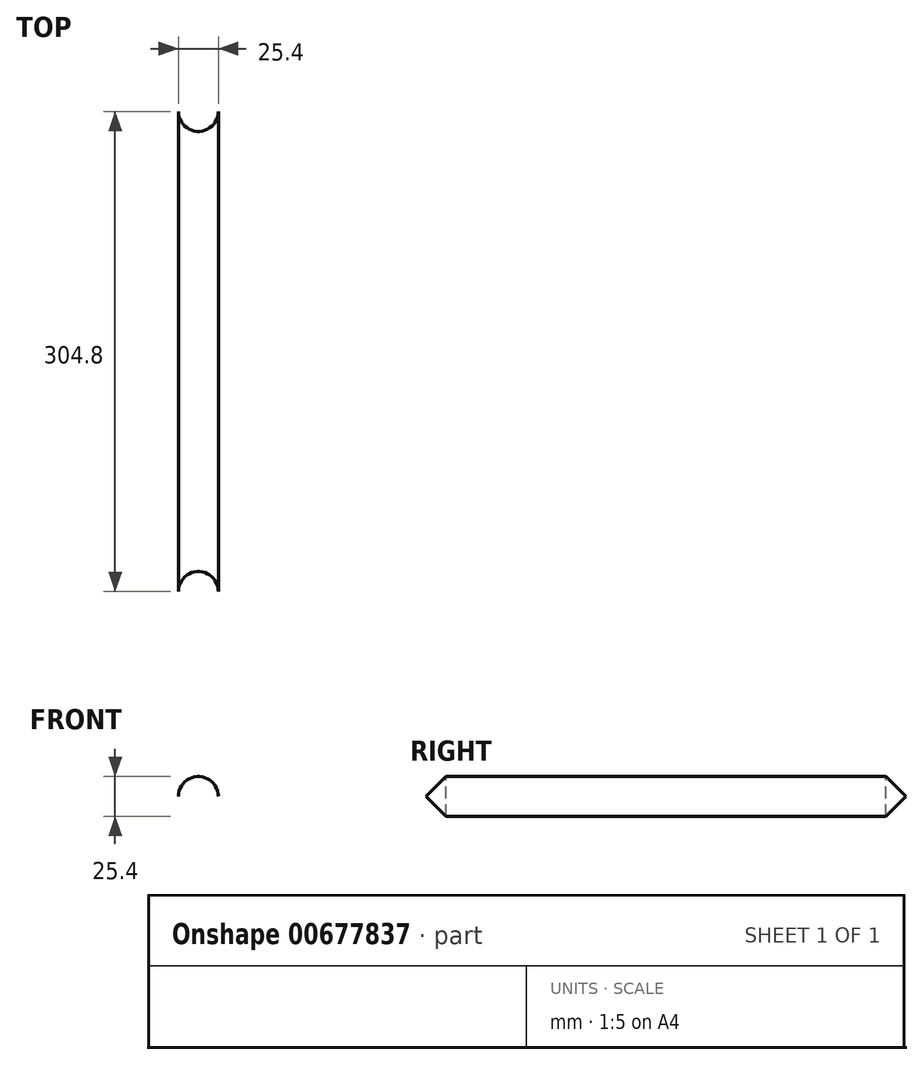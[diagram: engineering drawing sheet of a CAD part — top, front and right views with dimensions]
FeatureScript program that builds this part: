
annotation { "Feature Type Name" : "Feature", "Feature Type Description" : "" }
export const myFeature = defineFeature(function(context is Context, id is Id, definition is map)
    precondition{}
    {
        {
            var Q0;
            Q0=qCreatedBy(makeId("Front.planeOp"),FACE);
            var sketch = newSketch(context, id + "F0", { "sketchPlane" : qUnion([Q0])});
            skCircle(sketch, "E0", {"center": v(0, 0) * mm, "radius": 12.7 * mm});
            skSolve(sketch);
        }
        {
            var Q0;
            Q0=makeQuery(id+"F0.imprint","IMPRINT",FACE,{"disambiguationData":[TD([[makeQuery(id+"F0.imprint","IMPRINT",EDGE,{"derivedFrom":sQuery(id+"F0.wireOp",EDGE,"E0")}),1.0]])]});
            extrude(context, id + "F1", {"entities" : qUnion([Q0]), "depth" : 304.8 * mm, "offsetDistance" : 25.4 * mm});
        }
        {
            var Q0;
            Q0=qCreatedBy(makeId("Top.planeOp"),FACE);
            var sketch = newSketch(context, id + "F2", { "sketchPlane" : qUnion([Q0])});
            skCircle(sketch, "E1", {"center": v(0, 0) * mm, "radius": 12.7 * mm});
            skCircle(sketch, "E2", {"center": v(0, -304.8) * mm, "radius": 12.7 * mm});
            skSolve(sketch);
        }
        {
            var Q0;
            Q0 = qSketchRegion(id + "F2", true);
            extrude(context, id + "F3", {"entities" : qUnion([Q0]), "operationType" : NewBodyOperationType.REMOVE, "endBound" : BoundingType.THROUGH_ALL, "oppositeDirection" : true, "depth" : 25.4 * mm, "offsetDistance" : 25.4 * mm, "hasSecondDirection" : true, "secondDirectionBound" : SecondDirectionBoundingType.THROUGH_ALL, "secondDirectionOppositeDirection" : false, "secondDirectionDepth" : 25.4 * mm});
        }
    });
